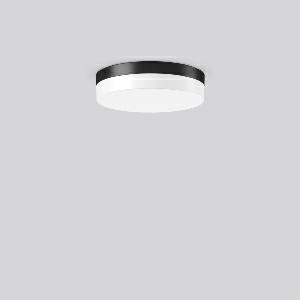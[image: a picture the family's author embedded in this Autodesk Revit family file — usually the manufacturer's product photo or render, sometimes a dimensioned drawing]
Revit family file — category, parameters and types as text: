
# Revit family: flat_slim_round_312629_0031_76_0bed
name_source: partatom
category: Lighting Fixtures
units: mm (PartAtom-declared; Revit-internal decimal feet)

## family parameters
Cut with Voids When Loaded = No
Host = Face
Light Source = No
Part Type = Normal
Room Calculation Point = No
Round Connector Dimension = Use Diameter
Shared = No

## types (1)
- MultiLumen 1 830 (1 x LED Modul 830, 1250 lm, 3000)
    Apparent Load = 13 VA
    CIE Flux Codes = 38 68 89 82 100
    Color Rendering = 80
    Color Temperature = 3000
    Default Elevation = 1800 mm
    Height = 75 mm
    Lamp = 1 x LED Modul 830
    Lamp Light Flux = 1250 lm
    Lamp count = 1
    Length = 300 mm
    Lifetime = 50000 h
    Luminous efficacy = 96 lm/W
    Manufacturer = RZB
    ModVariant = No
    Model = 312629.0031.76
    Mounting Place = Ceiling
    Mounting Type = Surface mounted
    Number of Poles = 1
    OnlyDefault = Yes
    Power Factor = 1
    Product Name = FLAT SLIM round
    Product group = Surface mounted ceiling and wall luminaires
    ProductGroupID = 305
    Protection Class = Protection class I
    Protection Degree = Degree of protection
    RLX_Detail_Level = 1
    RLX_Emergency_Light_Flux = 0 lm
    RLX_Emergency_Type = 0
    RLX_Emergency_Type_DB = No
    RlxData = <blob elided: 17617 chars, md5=692e4eee>
    Socket = socket
    Standby Power = 0 W
    System Light Flux = 1250 lm
    System Power = 13 W
    Type Comments = MultiLumen 1 830
    Type Image = 312629.0031.jpg
    URL = http://relux.com
    VarID = multilumen_1_830
    Voltage = 0 V
    Weight = 0.00 kg
    Width = 0 mm  [stored 0 ft]

note: [stored X ft] marks values corroborated as IEEE doubles in the binary element streams (Revit-internal decimal feet)

## geometry (parser evidence)
native form markers: Blend x4, Sweep x12
no freeform markers — native parametric forms only
